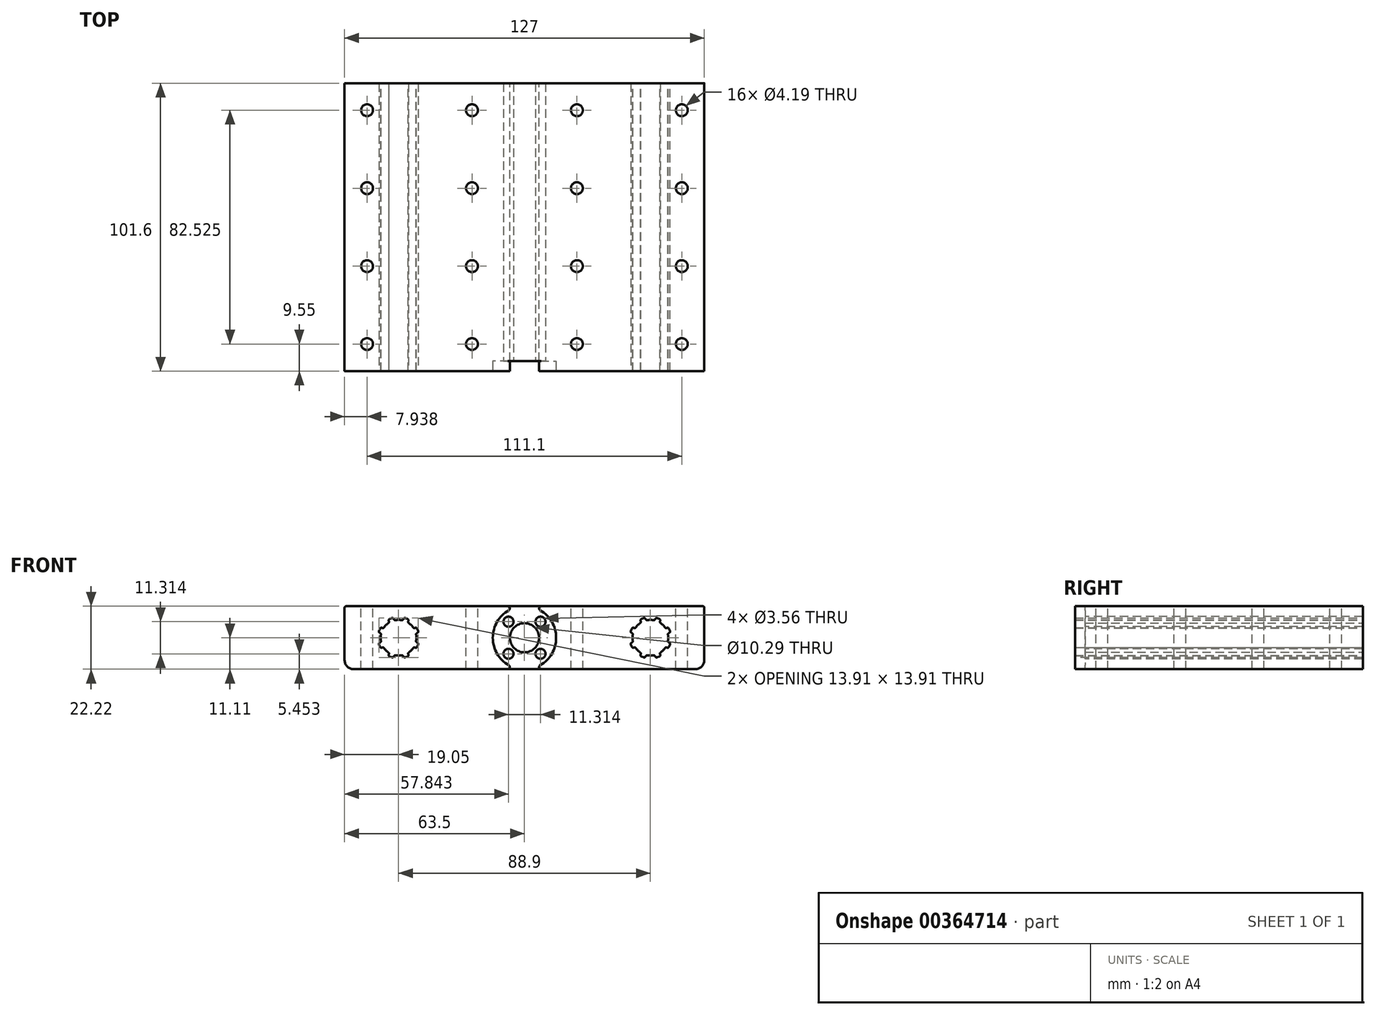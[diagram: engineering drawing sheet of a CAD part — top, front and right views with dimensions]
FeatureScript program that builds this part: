
annotation { "Feature Type Name" : "Feature", "Feature Type Description" : "" }
export const myFeature = defineFeature(function(context is Context, id is Id, definition is map)
    precondition{}
    {
        {
            var Q0;
            Q0=qCreatedBy(makeId("Front.planeOp"),FACE);
            var sketch = newSketch(context, id + "F0", { "sketchPlane" : qUnion([Q0])});
            skCircle(sketch, "E0", {"center": v(0, 0) * mm, "radius": 5.14 * mm});
            skCircle(sketch, "E1", {"center": v(44.45, 0) * mm, "radius": 6.3 * mm});
            skCircle(sketch, "E2", {"center": v(-44.45, 0) * mm, "radius": 6.3 * mm});
            skLineSegment(sketch, "E3", {"start": v(-44.45, 0) * mm, "end": v(0, 0) * mm, "construction": true});
            skLineSegment(sketch, "E4", {"start": v(44.45, 0) * mm, "end": v(0, 0) * mm, "construction": true});
            skLineSegment(sketch, "E5.bottom", {"start": v(-63.5, 11.11) * mm, "end": v(63.5, 11.11) * mm});
            skLineSegment(sketch, "E5.top", {"start": v(-63.5, -11.11) * mm, "end": v(63.5, -11.11) * mm});
            skLineSegment(sketch, "E5.left", {"start": v(-63.5, 11.11) * mm, "end": v(-63.5, -11.11) * mm});
            skLineSegment(sketch, "E5.right", {"start": v(63.5, 11.11) * mm, "end": v(63.5, -11.11) * mm});
            skSolve(sketch);
        }
        {
            var Q0;
            Q0 = qSketchRegion(id + "F0", true);
            extrude(context, id + "F1", {"entities" : qUnion([Q0]), "depth" : 101.6 * mm});
        }
        {
            var Q0;
            Q0=makeQuery(id+"F1.opExtrude","SWEPT_EDGE",EDGE,{"disambiguationData":[OSD([sQuery(id+"F0.wireOp",EDGE,"E5.top"),sQuery(id+"F0.wireOp",EDGE,"E5.left")])]});
            var Q1;
            Q1=makeQuery(id+"F1.opExtrude","SWEPT_EDGE",EDGE,{"disambiguationData":[OSD([sQuery(id+"F0.wireOp",EDGE,"E5.top"),sQuery(id+"F0.wireOp",EDGE,"E5.right")])]});
            fillet(context, id + "F2", {"entities" : qUnion([Q0, Q1]), "radius" : 3.17 * mm, "tangentPropagation" : true, "allowEdgeOverflow" : false});
        }
        {
            var Q0;
            Q0=makeQuery(id+"F1.opExtrude","CAP_FACE",FACE,{"disambiguationData":[OSD([sQuery(id+"F0.wireOp",EDGE,"E0"),sQuery(id+"F0.wireOp",EDGE,"E1"),sQuery(id+"F0.wireOp",EDGE,"E2"),sQuery(id+"F0.wireOp",EDGE,"E5.bottom"),sQuery(id+"F0.wireOp",EDGE,"E5.top"),sQuery(id+"F0.wireOp",EDGE,"E5.left"),sQuery(id+"F0.wireOp",EDGE,"E5.right")])],"isStart":false});
            var sketch = newSketch(context, id + "F3", { "sketchPlane" : qUnion([Q0])});
            skCircle(sketch, "E6", {"center": v(0, 0) * mm, "radius": 8 * mm, "construction": true});
            skCircle(sketch, "E7", {"center": v(-5.66, 5.66) * mm, "radius": 1.78 * mm});
            skCircle(sketch, "E8", {"center": v(5.66, 5.66) * mm, "radius": 1.78 * mm});
            skCircle(sketch, "E9", {"center": v(5.66, -5.66) * mm, "radius": 1.78 * mm});
            skCircle(sketch, "E10", {"center": v(-5.66, -5.66) * mm, "radius": 1.78 * mm});
            skLineSegment(sketch, "E11", {"start": v(-5.66, -5.66) * mm, "end": v(-5.66, 5.66) * mm, "construction": true});
            skLineSegment(sketch, "E12", {"start": v(5.66, 5.66) * mm, "end": v(-5.66, 5.66) * mm, "construction": true});
            skSolve(sketch);
        }
        {
            var Q0;
            Q0 = qSketchRegion(id + "F3", true);
            extrude(context, id + "F4", {"entities" : qUnion([Q0]), "operationType" : NewBodyOperationType.REMOVE, "endBound" : BoundingType.THROUGH_ALL, "oppositeDirection" : true, "depth" : 25.4 * mm});
        }
        {
            var Q0;
            Q0=makeQuery(id+"F1.opExtrude","SWEPT_FACE",FACE,{"disambiguationData":[OSD([sQuery(id+"F0.wireOp",EDGE,"E5.bottom")])]});
            var sketch = newSketch(context, id + "F5", { "sketchPlane" : qUnion([Q0])});
            skCircle(sketch, "E13", {"center": v(-55.56, -9.52) * mm, "radius": 2.1 * mm});
            skCircle(sketch, "E14.0.1.0", {"center": v(-55.56, -37.03) * mm, "radius": 2.1 * mm});
            skCircle(sketch, "E14.0.2.0", {"center": v(-55.56, -64.54) * mm, "radius": 2.1 * mm});
            skCircle(sketch, "E14.0.3.0", {"center": v(-55.56, -92.05) * mm, "radius": 2.1 * mm});
            skCircle(sketch, "E14.1.0.0", {"center": v(-18.53, -9.52) * mm, "radius": 2.1 * mm});
            skCircle(sketch, "E14.1.1.0", {"center": v(-18.53, -37.03) * mm, "radius": 2.1 * mm});
            skCircle(sketch, "E14.1.2.0", {"center": v(-18.53, -64.54) * mm, "radius": 2.1 * mm});
            skCircle(sketch, "E14.1.3.0", {"center": v(-18.53, -92.05) * mm, "radius": 2.1 * mm});
            skCircle(sketch, "E14.2.0.0", {"center": v(18.5, -9.52) * mm, "radius": 2.1 * mm});
            skCircle(sketch, "E14.2.1.0", {"center": v(18.5, -37.03) * mm, "radius": 2.1 * mm});
            skCircle(sketch, "E14.2.2.0", {"center": v(18.5, -64.54) * mm, "radius": 2.1 * mm});
            skCircle(sketch, "E14.2.3.0", {"center": v(18.5, -92.05) * mm, "radius": 2.1 * mm});
            skCircle(sketch, "E14.3.0.0", {"center": v(55.54, -9.52) * mm, "radius": 2.1 * mm});
            skCircle(sketch, "E14.3.1.0", {"center": v(55.54, -37.03) * mm, "radius": 2.1 * mm});
            skCircle(sketch, "E14.3.2.0", {"center": v(55.54, -64.54) * mm, "radius": 2.1 * mm});
            skCircle(sketch, "E14.3.3.0", {"center": v(55.54, -92.05) * mm, "radius": 2.1 * mm});
            skLineSegment(sketch, "E14.direction1", {"start": v(-55.56, -9.53) * mm, "end": v(-18.53, -9.53) * mm, "construction": true});
            skLineSegment(sketch, "E14.direction2", {"start": v(-55.56, -9.52) * mm, "end": v(-55.56, -37.03) * mm, "construction": true});
            skSolve(sketch);
        }
        {
            var Q0;
            Q0 = qSketchRegion(id + "F5", true);
            extrude(context, id + "F6", {"entities" : qUnion([Q0]), "operationType" : NewBodyOperationType.REMOVE, "oppositeDirection" : true, "depth" : 25.4 * mm, "offsetDistance" : 25.4 * mm});
        }
        {
            var Q0;
            Q0=makeQuery(id+"F1.opExtrude","CAP_FACE",FACE,{"disambiguationData":[OSD([sQuery(id+"F0.wireOp",EDGE,"E0"),sQuery(id+"F0.wireOp",EDGE,"E1"),sQuery(id+"F0.wireOp",EDGE,"E2"),sQuery(id+"F0.wireOp",EDGE,"E5.bottom"),sQuery(id+"F0.wireOp",EDGE,"E5.top"),sQuery(id+"F0.wireOp",EDGE,"E5.left"),sQuery(id+"F0.wireOp",EDGE,"E5.right")])],"isStart":false});
            var sketch = newSketch(context, id + "F7", { "sketchPlane" : qUnion([Q0])});
            skLineSegment(sketch, "E15.bottom", {"start": v(-50.83, 3.67) * mm, "end": v(-37.34, -1.91) * mm});
            skLineSegment(sketch, "E15.top", {"start": v(-51.56, 1.91) * mm, "end": v(-38.07, -3.67) * mm});
            skLineSegment(sketch, "E15.left", {"start": v(-50.83, 3.67) * mm, "end": v(-51.56, 1.91) * mm});
            skLineSegment(sketch, "E15.right", {"start": v(-37.34, -1.91) * mm, "end": v(-38.07, -3.67) * mm});
            skPoint(sketch, "E15.middle", {"position": v(-44.45, 0) * mm});
            skLineSegment(sketch, "E16", {"start": v(-44.45, 0) * mm, "end": v(-54.68, 0) * mm, "construction": true});
            skLineSegment(sketch, "E17.1.0", {"start": v(-46.36, 7.11) * mm, "end": v(-40.78, -6.38) * mm});
            skLineSegment(sketch, "E17.1.1", {"start": v(-40.78, -6.38) * mm, "end": v(-42.54, -7.11) * mm});
            skLineSegment(sketch, "E17.1.2", {"start": v(-48.12, 6.38) * mm, "end": v(-42.54, -7.11) * mm});
            skLineSegment(sketch, "E17.1.3", {"start": v(-46.36, 7.11) * mm, "end": v(-48.12, 6.38) * mm});
            skLineSegment(sketch, "E17.2.0", {"start": v(-40.78, 6.38) * mm, "end": v(-46.36, -7.11) * mm});
            skLineSegment(sketch, "E17.2.1", {"start": v(-46.36, -7.11) * mm, "end": v(-48.12, -6.38) * mm});
            skLineSegment(sketch, "E17.2.2", {"start": v(-42.54, 7.11) * mm, "end": v(-48.12, -6.38) * mm});
            skLineSegment(sketch, "E17.2.3", {"start": v(-40.78, 6.38) * mm, "end": v(-42.54, 7.11) * mm});
            skLineSegment(sketch, "E17.3.0", {"start": v(-37.34, 1.91) * mm, "end": v(-50.83, -3.67) * mm});
            skLineSegment(sketch, "E17.3.1", {"start": v(-50.83, -3.67) * mm, "end": v(-51.56, -1.91) * mm});
            skLineSegment(sketch, "E17.3.2", {"start": v(-38.07, 3.67) * mm, "end": v(-51.56, -1.91) * mm});
            skLineSegment(sketch, "E17.3.3", {"start": v(-37.34, 1.91) * mm, "end": v(-38.07, 3.67) * mm});
            skLineSegment(sketch, "E17.anchor1", {"start": v(-44.45, 0) * mm, "end": v(-50.83, 3.67) * mm, "construction": true});
            skLineSegment(sketch, "E17.anchor2", {"start": v(-44.45, 0) * mm, "end": v(-37.34, 1.91) * mm, "construction": true});
            skLineSegment(sketch, "E18.1.0.0", {"start": v(37.34, 1.91) * mm, "end": v(50.83, -3.67) * mm});
            skLineSegment(sketch, "E18.1.0.1", {"start": v(50.83, 3.67) * mm, "end": v(37.34, -1.91) * mm});
            skPoint(sketch, "E18.1.0.2", {"position": v(44.45, 0) * mm});
            skLineSegment(sketch, "E18.1.0.3", {"start": v(51.56, 1.91) * mm, "end": v(38.07, -3.67) * mm});
            skLineSegment(sketch, "E18.1.0.4", {"start": v(38.07, 3.67) * mm, "end": v(51.56, -1.91) * mm});
            skLineSegment(sketch, "E18.1.0.5", {"start": v(44.45, 0) * mm, "end": v(34.22, 0) * mm, "construction": true});
            skLineSegment(sketch, "E18.1.0.6", {"start": v(42.54, 7.11) * mm, "end": v(48.12, -6.38) * mm});
            skLineSegment(sketch, "E18.1.0.7", {"start": v(40.78, 6.38) * mm, "end": v(46.36, -7.11) * mm});
            skLineSegment(sketch, "E18.1.0.8", {"start": v(44.45, 0) * mm, "end": v(51.56, 1.91) * mm, "construction": true});
            skLineSegment(sketch, "E18.1.0.9", {"start": v(48.12, 6.38) * mm, "end": v(42.54, -7.11) * mm});
            skLineSegment(sketch, "E18.1.0.10", {"start": v(46.36, 7.11) * mm, "end": v(40.78, -6.38) * mm});
            skLineSegment(sketch, "E18.1.0.11", {"start": v(44.45, 0) * mm, "end": v(38.07, 3.67) * mm, "construction": true});
            skPoint(sketch, "E18.1.0.12", {"position": v(44.45, 0) * mm});
            skLineSegment(sketch, "E18.1.0.13", {"start": v(38.07, -3.67) * mm, "end": v(37.34, -1.91) * mm});
            skLineSegment(sketch, "E18.1.0.14", {"start": v(51.56, 1.91) * mm, "end": v(50.83, 3.67) * mm});
            skLineSegment(sketch, "E18.1.0.15", {"start": v(38.07, 3.67) * mm, "end": v(37.34, 1.91) * mm});
            skLineSegment(sketch, "E18.1.0.16", {"start": v(51.56, -1.91) * mm, "end": v(50.83, -3.67) * mm});
            skLineSegment(sketch, "E18.1.0.17", {"start": v(48.12, -6.38) * mm, "end": v(46.36, -7.11) * mm});
            skLineSegment(sketch, "E18.1.0.18", {"start": v(42.54, 7.11) * mm, "end": v(40.78, 6.38) * mm});
            skLineSegment(sketch, "E18.1.0.19", {"start": v(42.54, -7.11) * mm, "end": v(40.78, -6.38) * mm});
            skLineSegment(sketch, "E18.1.0.20", {"start": v(48.12, 6.38) * mm, "end": v(46.36, 7.11) * mm});
            skLineSegment(sketch, "E18.direction1", {"start": v(-54.68, 0) * mm, "end": v(34.22, 0) * mm, "construction": true});
            skSolve(sketch);
        }
        {
            var Q0;
            Q0 = qSketchRegion(id + "F7", true);
            extrude(context, id + "F8", {"entities" : qUnion([Q0]), "operationType" : NewBodyOperationType.REMOVE, "endBound" : BoundingType.THROUGH_ALL, "oppositeDirection" : true, "depth" : 25.4 * mm, "offsetDistance" : 25.4 * mm});
        }
        {
            var Q0;
            {var subQ0=sQuery(id+"F7.wireOp",EDGE,"E17.2.2");var subQ1=sQuery(id+"F0.wireOp",EDGE,"E2");Q0=makeQuery(id+"F8.boolean.opBoolean","INTERSECT",EDGE,{"derivedFrom":[makeQuery(id+"F1.opExtrude","SWEPT_FACE",FACE,{"disambiguationData":[OSD([subQ1])]}),makeQuery(id+"F8.opExtrude","SWEPT_FACE",FACE,{"disambiguationData":[OSD([subQ0]),TDD([makeQuery(id+"F7.imprint","IMPRINT",EDGE,{"disambiguationData":[TD([[makeQuery(id+"F7.imprint","INTERSECT",VERTEX,{"derivedFrom":[subQ0,sQuery(id+"F7.wireOp",EDGE,"E17.2.3")]}),-1.0]])],"derivedFrom":subQ0}),makeQuery(id+"F7.imprint","IMPRINT",EDGE,{"disambiguationData":[TD([[makeQuery(id+"F7.imprint","INTERSECT",VERTEX,{"derivedFrom":[sQuery(id+"F7.wireOp",EDGE,"E17.1.0"),subQ0]}),1.0]])],"derivedFrom":subQ0})])]})]});}
            var Q1;
            {var subQ0=sQuery(id+"F7.wireOp",EDGE,"E17.1.0");var subQ1=sQuery(id+"F0.wireOp",EDGE,"E2");Q1=makeQuery(id+"F8.boolean.opBoolean","INTERSECT",EDGE,{"derivedFrom":[makeQuery(id+"F1.opExtrude","SWEPT_FACE",FACE,{"disambiguationData":[OSD([subQ1])]}),makeQuery(id+"F8.opExtrude","SWEPT_FACE",FACE,{"disambiguationData":[OSD([subQ0]),TDD([makeQuery(id+"F7.imprint","IMPRINT",EDGE,{"disambiguationData":[TD([[makeQuery(id+"F7.imprint","INTERSECT",VERTEX,{"derivedFrom":[subQ0,sQuery(id+"F7.wireOp",EDGE,"E17.1.3")]}),-1.0]])],"derivedFrom":subQ0}),makeQuery(id+"F7.imprint","IMPRINT",EDGE,{"disambiguationData":[TD([[makeQuery(id+"F7.imprint","INTERSECT",VERTEX,{"derivedFrom":[subQ0,sQuery(id+"F7.wireOp",EDGE,"E17.2.2")]}),1.0]])],"derivedFrom":subQ0})])]})]});}
            var Q2;
            Q2=makeQuery(id+"F8.boolean.opBoolean","COPY",EDGE,{"derivedFrom":makeQuery(id+"F8.opExtrude","SWEPT_EDGE",EDGE,{"disambiguationData":[OSD([sQuery(id+"F7.wireOp",EDGE,"E17.1.0"),sQuery(id+"F7.wireOp",EDGE,"E17.1.3")])]})});
            var Q3;
            Q3=makeQuery(id+"F8.boolean.opBoolean","COPY",EDGE,{"derivedFrom":makeQuery(id+"F8.opExtrude","SWEPT_EDGE",EDGE,{"disambiguationData":[OSD([sQuery(id+"F7.wireOp",EDGE,"E17.1.2"),sQuery(id+"F7.wireOp",EDGE,"E17.1.3")])]})});
            var Q4;
            {var subQ0=sQuery(id+"F7.wireOp",EDGE,"E17.1.2");var subQ1=sQuery(id+"F0.wireOp",EDGE,"E2");Q4=makeQuery(id+"F8.boolean.opBoolean","INTERSECT",EDGE,{"derivedFrom":[makeQuery(id+"F1.opExtrude","SWEPT_FACE",FACE,{"disambiguationData":[OSD([subQ1])]}),makeQuery(id+"F8.opExtrude","SWEPT_FACE",FACE,{"disambiguationData":[OSD([subQ0]),TDD([makeQuery(id+"F7.imprint","IMPRINT",EDGE,{"disambiguationData":[TD([[makeQuery(id+"F7.imprint","INTERSECT",VERTEX,{"derivedFrom":[subQ0,sQuery(id+"F7.wireOp",EDGE,"E17.1.3")]}),-1.0]])],"derivedFrom":subQ0}),makeQuery(id+"F7.imprint","IMPRINT",EDGE,{"disambiguationData":[TD([[makeQuery(id+"F7.imprint","INTERSECT",VERTEX,{"derivedFrom":[sQuery(id+"F7.wireOp",EDGE,"E15.bottom"),subQ0]}),1.0]])],"derivedFrom":subQ0})])]})]});}
            var Q5;
            {var subQ0=sQuery(id+"F7.wireOp",EDGE,"E15.bottom");var subQ1=sQuery(id+"F0.wireOp",EDGE,"E2");Q5=makeQuery(id+"F8.boolean.opBoolean","INTERSECT",EDGE,{"derivedFrom":[makeQuery(id+"F1.opExtrude","SWEPT_FACE",FACE,{"disambiguationData":[OSD([subQ1])]}),makeQuery(id+"F8.opExtrude","SWEPT_FACE",FACE,{"disambiguationData":[OSD([subQ0]),TDD([makeQuery(id+"F7.imprint","IMPRINT",EDGE,{"disambiguationData":[TD([[makeQuery(id+"F7.imprint","INTERSECT",VERTEX,{"derivedFrom":[subQ0,sQuery(id+"F7.wireOp",EDGE,"E15.left")]}),-1.0]])],"derivedFrom":subQ0}),makeQuery(id+"F7.imprint","IMPRINT",EDGE,{"disambiguationData":[TD([[makeQuery(id+"F7.imprint","INTERSECT",VERTEX,{"derivedFrom":[subQ0,sQuery(id+"F7.wireOp",EDGE,"E17.1.2")]}),1.0]])],"derivedFrom":subQ0})])]})]});}
            var Q6;
            Q6=makeQuery(id+"F8.boolean.opBoolean","COPY",EDGE,{"derivedFrom":makeQuery(id+"F8.opExtrude","SWEPT_EDGE",EDGE,{"disambiguationData":[OSD([sQuery(id+"F7.wireOp",EDGE,"E15.bottom"),sQuery(id+"F7.wireOp",EDGE,"E15.left")])]})});
            var Q7;
            Q7=makeQuery(id+"F8.boolean.opBoolean","COPY",EDGE,{"derivedFrom":makeQuery(id+"F8.opExtrude","SWEPT_EDGE",EDGE,{"disambiguationData":[OSD([sQuery(id+"F7.wireOp",EDGE,"E15.top"),sQuery(id+"F7.wireOp",EDGE,"E15.left")])]})});
            var Q8;
            {var subQ0=sQuery(id+"F7.wireOp",EDGE,"E15.top");var subQ1=sQuery(id+"F0.wireOp",EDGE,"E2");Q8=makeQuery(id+"F8.boolean.opBoolean","INTERSECT",EDGE,{"derivedFrom":[makeQuery(id+"F1.opExtrude","SWEPT_FACE",FACE,{"disambiguationData":[OSD([subQ1])]}),makeQuery(id+"F8.opExtrude","SWEPT_FACE",FACE,{"disambiguationData":[OSD([subQ0]),TDD([makeQuery(id+"F7.imprint","IMPRINT",EDGE,{"disambiguationData":[TD([[makeQuery(id+"F7.imprint","INTERSECT",VERTEX,{"derivedFrom":[subQ0,sQuery(id+"F7.wireOp",EDGE,"E15.left")]}),-1.0]])],"derivedFrom":subQ0}),makeQuery(id+"F7.imprint","IMPRINT",EDGE,{"disambiguationData":[TD([[makeQuery(id+"F7.imprint","INTERSECT",VERTEX,{"derivedFrom":[subQ0,sQuery(id+"F7.wireOp",EDGE,"E17.3.2")]}),1.0]])],"derivedFrom":subQ0})])]})]});}
            var Q9;
            {var subQ0=sQuery(id+"F7.wireOp",EDGE,"E17.3.2");var subQ1=sQuery(id+"F0.wireOp",EDGE,"E2");Q9=makeQuery(id+"F8.boolean.opBoolean","INTERSECT",EDGE,{"derivedFrom":[makeQuery(id+"F1.opExtrude","SWEPT_FACE",FACE,{"disambiguationData":[OSD([subQ1])]}),makeQuery(id+"F8.opExtrude","SWEPT_FACE",FACE,{"disambiguationData":[OSD([subQ0]),TDD([makeQuery(id+"F7.imprint","IMPRINT",EDGE,{"disambiguationData":[TD([[makeQuery(id+"F7.imprint","INTERSECT",VERTEX,{"derivedFrom":[sQuery(id+"F7.wireOp",EDGE,"E15.top"),subQ0]}),-1.0]])],"derivedFrom":subQ0}),makeQuery(id+"F7.imprint","IMPRINT",EDGE,{"disambiguationData":[TD([[makeQuery(id+"F7.imprint","INTERSECT",VERTEX,{"derivedFrom":[sQuery(id+"F7.wireOp",EDGE,"E17.3.1"),subQ0]}),1.0]])],"derivedFrom":subQ0})])]})]});}
            var Q10;
            Q10=makeQuery(id+"F8.boolean.opBoolean","COPY",EDGE,{"derivedFrom":makeQuery(id+"F8.opExtrude","SWEPT_EDGE",EDGE,{"disambiguationData":[OSD([sQuery(id+"F7.wireOp",EDGE,"E17.3.1"),sQuery(id+"F7.wireOp",EDGE,"E17.3.2")])]})});
            var Q11;
            Q11=makeQuery(id+"F8.boolean.opBoolean","COPY",EDGE,{"derivedFrom":makeQuery(id+"F8.opExtrude","SWEPT_EDGE",EDGE,{"disambiguationData":[OSD([sQuery(id+"F7.wireOp",EDGE,"E17.3.0"),sQuery(id+"F7.wireOp",EDGE,"E17.3.1")])]})});
            var Q12;
            {var subQ0=sQuery(id+"F7.wireOp",EDGE,"E17.3.0");var subQ1=sQuery(id+"F0.wireOp",EDGE,"E2");Q12=makeQuery(id+"F8.boolean.opBoolean","INTERSECT",EDGE,{"derivedFrom":[makeQuery(id+"F1.opExtrude","SWEPT_FACE",FACE,{"disambiguationData":[OSD([subQ1])]}),makeQuery(id+"F8.opExtrude","SWEPT_FACE",FACE,{"disambiguationData":[OSD([subQ0]),TDD([makeQuery(id+"F7.imprint","IMPRINT",EDGE,{"disambiguationData":[TD([[makeQuery(id+"F7.imprint","INTERSECT",VERTEX,{"derivedFrom":[sQuery(id+"F7.wireOp",EDGE,"E17.2.2"),subQ0]}),-1.0]])],"derivedFrom":subQ0}),makeQuery(id+"F7.imprint","IMPRINT",EDGE,{"disambiguationData":[TD([[makeQuery(id+"F7.imprint","INTERSECT",VERTEX,{"derivedFrom":[subQ0,sQuery(id+"F7.wireOp",EDGE,"E17.3.1")]}),1.0]])],"derivedFrom":subQ0})])]})]});}
            var Q13;
            Q13=makeQuery(id+"F8.boolean.opBoolean","COPY",EDGE,{"derivedFrom":makeQuery(id+"F8.opExtrude","SWEPT_EDGE",EDGE,{"disambiguationData":[OSD([sQuery(id+"F7.wireOp",EDGE,"E17.2.1"),sQuery(id+"F7.wireOp",EDGE,"E17.2.2")])]})});
            var Q14;
            {var subQ0=sQuery(id+"F7.wireOp",EDGE,"E17.2.2");var subQ1=sQuery(id+"F0.wireOp",EDGE,"E2");Q14=makeQuery(id+"F8.boolean.opBoolean","INTERSECT",EDGE,{"derivedFrom":[makeQuery(id+"F1.opExtrude","SWEPT_FACE",FACE,{"disambiguationData":[OSD([subQ1])]}),makeQuery(id+"F8.opExtrude","SWEPT_FACE",FACE,{"disambiguationData":[OSD([subQ0]),TDD([makeQuery(id+"F7.imprint","IMPRINT",EDGE,{"disambiguationData":[TD([[makeQuery(id+"F7.imprint","INTERSECT",VERTEX,{"derivedFrom":[subQ0,sQuery(id+"F7.wireOp",EDGE,"E17.3.0")]}),-1.0]])],"derivedFrom":subQ0}),makeQuery(id+"F7.imprint","IMPRINT",EDGE,{"disambiguationData":[TD([[makeQuery(id+"F7.imprint","INTERSECT",VERTEX,{"derivedFrom":[sQuery(id+"F7.wireOp",EDGE,"E17.2.1"),subQ0]}),1.0]])],"derivedFrom":subQ0})])]})]});}
            var Q15;
            Q15=makeQuery(id+"F8.boolean.opBoolean","COPY",EDGE,{"derivedFrom":makeQuery(id+"F8.opExtrude","SWEPT_EDGE",EDGE,{"disambiguationData":[OSD([sQuery(id+"F7.wireOp",EDGE,"E17.2.0"),sQuery(id+"F7.wireOp",EDGE,"E17.2.1")])]})});
            var Q16;
            {var subQ0=sQuery(id+"F7.wireOp",EDGE,"E17.2.0");var subQ1=sQuery(id+"F0.wireOp",EDGE,"E2");Q16=makeQuery(id+"F8.boolean.opBoolean","INTERSECT",EDGE,{"derivedFrom":[makeQuery(id+"F1.opExtrude","SWEPT_FACE",FACE,{"disambiguationData":[OSD([subQ1])]}),makeQuery(id+"F8.opExtrude","SWEPT_FACE",FACE,{"disambiguationData":[OSD([subQ0]),TDD([makeQuery(id+"F7.imprint","IMPRINT",EDGE,{"disambiguationData":[TD([[makeQuery(id+"F7.imprint","INTERSECT",VERTEX,{"derivedFrom":[sQuery(id+"F7.wireOp",EDGE,"E17.1.2"),subQ0]}),-1.0]])],"derivedFrom":subQ0}),makeQuery(id+"F7.imprint","IMPRINT",EDGE,{"disambiguationData":[TD([[makeQuery(id+"F7.imprint","INTERSECT",VERTEX,{"derivedFrom":[subQ0,sQuery(id+"F7.wireOp",EDGE,"E17.2.1")]}),1.0]])],"derivedFrom":subQ0})])]})]});}
            var Q17;
            Q17=makeQuery(id+"F8.boolean.opBoolean","COPY",EDGE,{"derivedFrom":makeQuery(id+"F8.opExtrude","SWEPT_EDGE",EDGE,{"disambiguationData":[OSD([sQuery(id+"F7.wireOp",EDGE,"E17.1.1"),sQuery(id+"F7.wireOp",EDGE,"E17.1.2")])]})});
            var Q18;
            {var subQ0=sQuery(id+"F7.wireOp",EDGE,"E17.1.2");var subQ1=sQuery(id+"F0.wireOp",EDGE,"E2");Q18=makeQuery(id+"F8.boolean.opBoolean","INTERSECT",EDGE,{"derivedFrom":[makeQuery(id+"F1.opExtrude","SWEPT_FACE",FACE,{"disambiguationData":[OSD([subQ1])]}),makeQuery(id+"F8.opExtrude","SWEPT_FACE",FACE,{"disambiguationData":[OSD([subQ0]),TDD([makeQuery(id+"F7.imprint","IMPRINT",EDGE,{"disambiguationData":[TD([[makeQuery(id+"F7.imprint","INTERSECT",VERTEX,{"derivedFrom":[subQ0,sQuery(id+"F7.wireOp",EDGE,"E17.2.0")]}),-1.0]])],"derivedFrom":subQ0}),makeQuery(id+"F7.imprint","IMPRINT",EDGE,{"disambiguationData":[TD([[makeQuery(id+"F7.imprint","INTERSECT",VERTEX,{"derivedFrom":[sQuery(id+"F7.wireOp",EDGE,"E17.1.1"),subQ0]}),1.0]])],"derivedFrom":subQ0})])]})]});}
            var Q19;
            Q19=makeQuery(id+"F8.boolean.opBoolean","COPY",EDGE,{"derivedFrom":makeQuery(id+"F8.opExtrude","SWEPT_EDGE",EDGE,{"disambiguationData":[OSD([sQuery(id+"F7.wireOp",EDGE,"E17.1.0"),sQuery(id+"F7.wireOp",EDGE,"E17.1.1")])]})});
            var Q20;
            {var subQ0=sQuery(id+"F7.wireOp",EDGE,"E17.1.0");var subQ1=sQuery(id+"F0.wireOp",EDGE,"E2");Q20=makeQuery(id+"F8.boolean.opBoolean","INTERSECT",EDGE,{"derivedFrom":[makeQuery(id+"F1.opExtrude","SWEPT_FACE",FACE,{"disambiguationData":[OSD([subQ1])]}),makeQuery(id+"F8.opExtrude","SWEPT_FACE",FACE,{"disambiguationData":[OSD([subQ0]),TDD([makeQuery(id+"F7.imprint","IMPRINT",EDGE,{"disambiguationData":[TD([[makeQuery(id+"F7.imprint","INTERSECT",VERTEX,{"derivedFrom":[sQuery(id+"F7.wireOp",EDGE,"E15.top"),subQ0]}),-1.0]])],"derivedFrom":subQ0}),makeQuery(id+"F7.imprint","IMPRINT",EDGE,{"disambiguationData":[TD([[makeQuery(id+"F7.imprint","INTERSECT",VERTEX,{"derivedFrom":[subQ0,sQuery(id+"F7.wireOp",EDGE,"E17.1.1")]}),1.0]])],"derivedFrom":subQ0})])]})]});}
            var Q21;
            Q21=makeQuery(id+"F8.boolean.opBoolean","COPY",EDGE,{"derivedFrom":makeQuery(id+"F8.opExtrude","SWEPT_EDGE",EDGE,{"disambiguationData":[OSD([sQuery(id+"F7.wireOp",EDGE,"E15.top"),sQuery(id+"F7.wireOp",EDGE,"E15.right")])]})});
            var Q22;
            {var subQ0=sQuery(id+"F7.wireOp",EDGE,"E15.top");var subQ1=sQuery(id+"F0.wireOp",EDGE,"E2");Q22=makeQuery(id+"F8.boolean.opBoolean","INTERSECT",EDGE,{"derivedFrom":[makeQuery(id+"F1.opExtrude","SWEPT_FACE",FACE,{"disambiguationData":[OSD([subQ1])]}),makeQuery(id+"F8.opExtrude","SWEPT_FACE",FACE,{"disambiguationData":[OSD([subQ0]),TDD([makeQuery(id+"F7.imprint","IMPRINT",EDGE,{"disambiguationData":[TD([[makeQuery(id+"F7.imprint","INTERSECT",VERTEX,{"derivedFrom":[subQ0,sQuery(id+"F7.wireOp",EDGE,"E17.1.0")]}),-1.0]])],"derivedFrom":subQ0}),makeQuery(id+"F7.imprint","IMPRINT",EDGE,{"disambiguationData":[TD([[makeQuery(id+"F7.imprint","INTERSECT",VERTEX,{"derivedFrom":[subQ0,sQuery(id+"F7.wireOp",EDGE,"E15.right")]}),1.0]])],"derivedFrom":subQ0})])]})]});}
            var Q23;
            Q23=makeQuery(id+"F8.boolean.opBoolean","COPY",EDGE,{"derivedFrom":makeQuery(id+"F8.opExtrude","SWEPT_EDGE",EDGE,{"disambiguationData":[OSD([sQuery(id+"F7.wireOp",EDGE,"E15.bottom"),sQuery(id+"F7.wireOp",EDGE,"E15.right")])]})});
            var Q24;
            {var subQ0=sQuery(id+"F7.wireOp",EDGE,"E15.bottom");var subQ1=sQuery(id+"F0.wireOp",EDGE,"E2");Q24=makeQuery(id+"F8.boolean.opBoolean","INTERSECT",EDGE,{"derivedFrom":[makeQuery(id+"F1.opExtrude","SWEPT_FACE",FACE,{"disambiguationData":[OSD([subQ1])]}),makeQuery(id+"F8.opExtrude","SWEPT_FACE",FACE,{"disambiguationData":[OSD([subQ0]),TDD([makeQuery(id+"F7.imprint","IMPRINT",EDGE,{"disambiguationData":[TD([[makeQuery(id+"F7.imprint","INTERSECT",VERTEX,{"derivedFrom":[subQ0,sQuery(id+"F7.wireOp",EDGE,"E17.3.0")]}),-1.0]])],"derivedFrom":subQ0}),makeQuery(id+"F7.imprint","IMPRINT",EDGE,{"disambiguationData":[TD([[makeQuery(id+"F7.imprint","INTERSECT",VERTEX,{"derivedFrom":[subQ0,sQuery(id+"F7.wireOp",EDGE,"E15.right")]}),1.0]])],"derivedFrom":subQ0})])]})]});}
            var Q25;
            {var subQ0=sQuery(id+"F7.wireOp",EDGE,"E17.3.0");var subQ1=sQuery(id+"F0.wireOp",EDGE,"E2");Q25=makeQuery(id+"F8.boolean.opBoolean","INTERSECT",EDGE,{"derivedFrom":[makeQuery(id+"F1.opExtrude","SWEPT_FACE",FACE,{"disambiguationData":[OSD([subQ1])]}),makeQuery(id+"F8.opExtrude","SWEPT_FACE",FACE,{"disambiguationData":[OSD([subQ0]),TDD([makeQuery(id+"F7.imprint","IMPRINT",EDGE,{"disambiguationData":[TD([[makeQuery(id+"F7.imprint","INTERSECT",VERTEX,{"derivedFrom":[subQ0,sQuery(id+"F7.wireOp",EDGE,"E17.3.3")]}),-1.0]])],"derivedFrom":subQ0}),makeQuery(id+"F7.imprint","IMPRINT",EDGE,{"disambiguationData":[TD([[makeQuery(id+"F7.imprint","INTERSECT",VERTEX,{"derivedFrom":[sQuery(id+"F7.wireOp",EDGE,"E15.bottom"),subQ0]}),1.0]])],"derivedFrom":subQ0})])]})]});}
            var Q26;
            Q26=makeQuery(id+"F8.boolean.opBoolean","COPY",EDGE,{"derivedFrom":makeQuery(id+"F8.opExtrude","SWEPT_EDGE",EDGE,{"disambiguationData":[OSD([sQuery(id+"F7.wireOp",EDGE,"E17.3.0"),sQuery(id+"F7.wireOp",EDGE,"E17.3.3")])]})});
            var Q27;
            Q27=makeQuery(id+"F8.boolean.opBoolean","COPY",EDGE,{"derivedFrom":makeQuery(id+"F8.opExtrude","SWEPT_EDGE",EDGE,{"disambiguationData":[OSD([sQuery(id+"F7.wireOp",EDGE,"E17.3.2"),sQuery(id+"F7.wireOp",EDGE,"E17.3.3")])]})});
            var Q28;
            {var subQ0=sQuery(id+"F7.wireOp",EDGE,"E17.3.2");var subQ1=sQuery(id+"F0.wireOp",EDGE,"E2");Q28=makeQuery(id+"F8.boolean.opBoolean","INTERSECT",EDGE,{"derivedFrom":[makeQuery(id+"F1.opExtrude","SWEPT_FACE",FACE,{"disambiguationData":[OSD([subQ1])]}),makeQuery(id+"F8.opExtrude","SWEPT_FACE",FACE,{"disambiguationData":[OSD([subQ0]),TDD([makeQuery(id+"F7.imprint","IMPRINT",EDGE,{"disambiguationData":[TD([[makeQuery(id+"F7.imprint","INTERSECT",VERTEX,{"derivedFrom":[subQ0,sQuery(id+"F7.wireOp",EDGE,"E17.3.3")]}),-1.0]])],"derivedFrom":subQ0}),makeQuery(id+"F7.imprint","IMPRINT",EDGE,{"disambiguationData":[TD([[makeQuery(id+"F7.imprint","INTERSECT",VERTEX,{"derivedFrom":[sQuery(id+"F7.wireOp",EDGE,"E17.2.0"),subQ0]}),1.0]])],"derivedFrom":subQ0})])]})]});}
            var Q29;
            Q29=makeQuery(id+"F8.boolean.opBoolean","COPY",EDGE,{"derivedFrom":makeQuery(id+"F8.opExtrude","SWEPT_EDGE",EDGE,{"disambiguationData":[OSD([sQuery(id+"F7.wireOp",EDGE,"E17.2.0"),sQuery(id+"F7.wireOp",EDGE,"E17.2.3")])]})});
            var Q30;
            {var subQ0=sQuery(id+"F7.wireOp",EDGE,"E17.2.0");var subQ1=sQuery(id+"F0.wireOp",EDGE,"E2");Q30=makeQuery(id+"F8.boolean.opBoolean","INTERSECT",EDGE,{"derivedFrom":[makeQuery(id+"F1.opExtrude","SWEPT_FACE",FACE,{"disambiguationData":[OSD([subQ1])]}),makeQuery(id+"F8.opExtrude","SWEPT_FACE",FACE,{"disambiguationData":[OSD([subQ0]),TDD([makeQuery(id+"F7.imprint","IMPRINT",EDGE,{"disambiguationData":[TD([[makeQuery(id+"F7.imprint","INTERSECT",VERTEX,{"derivedFrom":[subQ0,sQuery(id+"F7.wireOp",EDGE,"E17.2.3")]}),-1.0]])],"derivedFrom":subQ0}),makeQuery(id+"F7.imprint","IMPRINT",EDGE,{"disambiguationData":[TD([[makeQuery(id+"F7.imprint","INTERSECT",VERTEX,{"derivedFrom":[subQ0,sQuery(id+"F7.wireOp",EDGE,"E17.3.2")]}),1.0]])],"derivedFrom":subQ0})])]})]});}
            var Q31;
            Q31=makeQuery(id+"F8.boolean.opBoolean","COPY",EDGE,{"derivedFrom":makeQuery(id+"F8.opExtrude","SWEPT_EDGE",EDGE,{"disambiguationData":[OSD([sQuery(id+"F7.wireOp",EDGE,"E17.2.2"),sQuery(id+"F7.wireOp",EDGE,"E17.2.3")])]})});
            fillet(context, id + "F9", {"entities" : qUnion([Q0, Q1, Q2, Q3, Q4, Q5, Q6, Q7, Q8, Q9, Q10, Q11, Q12, Q13, Q14, Q15, Q16, Q17, Q18, Q19, Q20, Q21, Q22, Q23, Q24, Q25, Q26, Q27, Q28, Q29, Q30, Q31]), "radius" : 0.5 * mm, "allowEdgeOverflow" : false});
        }
        {
            var Q0;
            Q0=makeQuery(id+"F8.boolean.opBoolean","COPY",EDGE,{"derivedFrom":makeQuery(id+"F8.opExtrude","SWEPT_EDGE",EDGE,{"disambiguationData":[OSD([sQuery(id+"F7.wireOp",EDGE,"E18.1.0.7"),sQuery(id+"F7.wireOp",EDGE,"E18.1.0.17")])]})});
            var Q1;
            {var subQ0=sQuery(id+"F7.wireOp",EDGE,"E18.1.0.7");var subQ1=sQuery(id+"F0.wireOp",EDGE,"E1");Q1=makeQuery(id+"F8.boolean.opBoolean","INTERSECT",EDGE,{"derivedFrom":[makeQuery(id+"F1.opExtrude","SWEPT_FACE",FACE,{"disambiguationData":[OSD([subQ1])]}),makeQuery(id+"F8.opExtrude","SWEPT_FACE",FACE,{"disambiguationData":[OSD([subQ0]),TDD([makeQuery(id+"F7.imprint","IMPRINT",EDGE,{"disambiguationData":[TD([[makeQuery(id+"F7.imprint","INTERSECT",VERTEX,{"derivedFrom":[subQ0,sQuery(id+"F7.wireOp",EDGE,"E18.1.0.9")]}),-1.0]])],"derivedFrom":subQ0}),makeQuery(id+"F7.imprint","IMPRINT",EDGE,{"disambiguationData":[TD([[makeQuery(id+"F7.imprint","INTERSECT",VERTEX,{"derivedFrom":[subQ0,sQuery(id+"F7.wireOp",EDGE,"E18.1.0.17")]}),1.0]])],"derivedFrom":subQ0})])]})]});}
            var Q2;
            {var subQ0=sQuery(id+"F7.wireOp",EDGE,"E18.1.0.9");var subQ1=sQuery(id+"F0.wireOp",EDGE,"E1");Q2=makeQuery(id+"F8.boolean.opBoolean","INTERSECT",EDGE,{"derivedFrom":[makeQuery(id+"F1.opExtrude","SWEPT_FACE",FACE,{"disambiguationData":[OSD([subQ1])]}),makeQuery(id+"F8.opExtrude","SWEPT_FACE",FACE,{"disambiguationData":[OSD([subQ0]),TDD([makeQuery(id+"F7.imprint","IMPRINT",EDGE,{"disambiguationData":[TD([[makeQuery(id+"F7.imprint","INTERSECT",VERTEX,{"derivedFrom":[sQuery(id+"F7.wireOp",EDGE,"E18.1.0.7"),subQ0]}),-1.0]])],"derivedFrom":subQ0}),makeQuery(id+"F7.imprint","IMPRINT",EDGE,{"disambiguationData":[TD([[makeQuery(id+"F7.imprint","INTERSECT",VERTEX,{"derivedFrom":[subQ0,sQuery(id+"F7.wireOp",EDGE,"E18.1.0.19")]}),1.0]])],"derivedFrom":subQ0})])]})]});}
            var Q3;
            {var subQ0=sQuery(id+"F7.wireOp",EDGE,"E18.1.0.10");var subQ1=sQuery(id+"F0.wireOp",EDGE,"E1");Q3=makeQuery(id+"F8.boolean.opBoolean","INTERSECT",EDGE,{"derivedFrom":[makeQuery(id+"F1.opExtrude","SWEPT_FACE",FACE,{"disambiguationData":[OSD([subQ1])]}),makeQuery(id+"F8.opExtrude","SWEPT_FACE",FACE,{"disambiguationData":[OSD([subQ0]),TDD([makeQuery(id+"F7.imprint","IMPRINT",EDGE,{"disambiguationData":[TD([[makeQuery(id+"F7.imprint","INTERSECT",VERTEX,{"derivedFrom":[sQuery(id+"F7.wireOp",EDGE,"E18.1.0.3"),subQ0]}),-1.0]])],"derivedFrom":subQ0}),makeQuery(id+"F7.imprint","IMPRINT",EDGE,{"disambiguationData":[TD([[makeQuery(id+"F7.imprint","INTERSECT",VERTEX,{"derivedFrom":[subQ0,sQuery(id+"F7.wireOp",EDGE,"E18.1.0.19")]}),1.0]])],"derivedFrom":subQ0})])]})]});}
            var Q4;
            Q4=makeQuery(id+"F8.boolean.opBoolean","COPY",EDGE,{"derivedFrom":makeQuery(id+"F8.opExtrude","SWEPT_EDGE",EDGE,{"disambiguationData":[OSD([sQuery(id+"F7.wireOp",EDGE,"E18.1.0.10"),sQuery(id+"F7.wireOp",EDGE,"E18.1.0.19")])]})});
            var Q5;
            {var subQ0=sQuery(id+"F7.wireOp",EDGE,"E18.1.0.3");var subQ1=sQuery(id+"F0.wireOp",EDGE,"E1");Q5=makeQuery(id+"F8.boolean.opBoolean","INTERSECT",EDGE,{"derivedFrom":[makeQuery(id+"F1.opExtrude","SWEPT_FACE",FACE,{"disambiguationData":[OSD([subQ1])]}),makeQuery(id+"F8.opExtrude","SWEPT_FACE",FACE,{"disambiguationData":[OSD([subQ0]),TDD([makeQuery(id+"F7.imprint","IMPRINT",EDGE,{"disambiguationData":[TD([[makeQuery(id+"F7.imprint","INTERSECT",VERTEX,{"derivedFrom":[subQ0,sQuery(id+"F7.wireOp",EDGE,"E18.1.0.10")]}),-1.0]])],"derivedFrom":subQ0}),makeQuery(id+"F7.imprint","IMPRINT",EDGE,{"disambiguationData":[TD([[makeQuery(id+"F7.imprint","INTERSECT",VERTEX,{"derivedFrom":[subQ0,sQuery(id+"F7.wireOp",EDGE,"E18.1.0.13")]}),1.0]])],"derivedFrom":subQ0})])]})]});}
            var Q6;
            Q6=makeQuery(id+"F8.boolean.opBoolean","COPY",EDGE,{"derivedFrom":makeQuery(id+"F8.opExtrude","SWEPT_EDGE",EDGE,{"disambiguationData":[OSD([sQuery(id+"F7.wireOp",EDGE,"E18.1.0.3"),sQuery(id+"F7.wireOp",EDGE,"E18.1.0.13")])]})});
            var Q7;
            {var subQ0=sQuery(id+"F7.wireOp",EDGE,"E18.1.0.6");var subQ1=sQuery(id+"F0.wireOp",EDGE,"E1");Q7=makeQuery(id+"F8.boolean.opBoolean","INTERSECT",EDGE,{"derivedFrom":[makeQuery(id+"F1.opExtrude","SWEPT_FACE",FACE,{"disambiguationData":[OSD([subQ1])]}),makeQuery(id+"F8.opExtrude","SWEPT_FACE",FACE,{"disambiguationData":[OSD([subQ0]),TDD([makeQuery(id+"F7.imprint","IMPRINT",EDGE,{"disambiguationData":[TD([[makeQuery(id+"F7.imprint","INTERSECT",VERTEX,{"derivedFrom":[sQuery(id+"F7.wireOp",EDGE,"E18.1.0.0"),subQ0]}),-1.0]])],"derivedFrom":subQ0}),makeQuery(id+"F7.imprint","IMPRINT",EDGE,{"disambiguationData":[TD([[makeQuery(id+"F7.imprint","INTERSECT",VERTEX,{"derivedFrom":[subQ0,sQuery(id+"F7.wireOp",EDGE,"E18.1.0.17")]}),1.0]])],"derivedFrom":subQ0})])]})]});}
            var Q8;
            Q8=makeQuery(id+"F8.boolean.opBoolean","COPY",EDGE,{"derivedFrom":makeQuery(id+"F8.opExtrude","SWEPT_EDGE",EDGE,{"disambiguationData":[OSD([sQuery(id+"F7.wireOp",EDGE,"E18.1.0.6"),sQuery(id+"F7.wireOp",EDGE,"E18.1.0.17")])]})});
            var Q9;
            Q9=makeQuery(id+"F8.boolean.opBoolean","COPY",EDGE,{"derivedFrom":makeQuery(id+"F8.opExtrude","SWEPT_EDGE",EDGE,{"disambiguationData":[OSD([sQuery(id+"F7.wireOp",EDGE,"E18.1.0.9"),sQuery(id+"F7.wireOp",EDGE,"E18.1.0.19")])]})});
            var Q10;
            Q10=makeQuery(id+"F8.boolean.opBoolean","COPY",EDGE,{"derivedFrom":makeQuery(id+"F8.opExtrude","SWEPT_EDGE",EDGE,{"disambiguationData":[OSD([sQuery(id+"F7.wireOp",EDGE,"E18.1.0.0"),sQuery(id+"F7.wireOp",EDGE,"E18.1.0.15")])]})});
            var Q11;
            {var subQ0=sQuery(id+"F7.wireOp",EDGE,"E18.1.0.0");var subQ1=sQuery(id+"F0.wireOp",EDGE,"E1");Q11=makeQuery(id+"F8.boolean.opBoolean","INTERSECT",EDGE,{"derivedFrom":[makeQuery(id+"F1.opExtrude","SWEPT_FACE",FACE,{"disambiguationData":[OSD([subQ1])]}),makeQuery(id+"F8.opExtrude","SWEPT_FACE",FACE,{"disambiguationData":[OSD([subQ0]),TDD([makeQuery(id+"F7.imprint","IMPRINT",EDGE,{"disambiguationData":[TD([[makeQuery(id+"F7.imprint","INTERSECT",VERTEX,{"derivedFrom":[subQ0,sQuery(id+"F7.wireOp",EDGE,"E18.1.0.15")]}),-1.0]])],"derivedFrom":subQ0}),makeQuery(id+"F7.imprint","IMPRINT",EDGE,{"disambiguationData":[TD([[makeQuery(id+"F7.imprint","INTERSECT",VERTEX,{"derivedFrom":[subQ0,sQuery(id+"F7.wireOp",EDGE,"E18.1.0.1")]}),1.0]])],"derivedFrom":subQ0})])]})]});}
            var Q12;
            {var subQ0=sQuery(id+"F7.wireOp",EDGE,"E18.1.0.1");var subQ1=sQuery(id+"F0.wireOp",EDGE,"E1");Q12=makeQuery(id+"F8.boolean.opBoolean","INTERSECT",EDGE,{"derivedFrom":[makeQuery(id+"F1.opExtrude","SWEPT_FACE",FACE,{"disambiguationData":[OSD([subQ1])]}),makeQuery(id+"F8.opExtrude","SWEPT_FACE",FACE,{"disambiguationData":[OSD([subQ0]),TDD([makeQuery(id+"F7.imprint","IMPRINT",EDGE,{"disambiguationData":[TD([[makeQuery(id+"F7.imprint","INTERSECT",VERTEX,{"derivedFrom":[sQuery(id+"F7.wireOp",EDGE,"E18.1.0.0"),subQ0]}),-1.0]])],"derivedFrom":subQ0}),makeQuery(id+"F7.imprint","IMPRINT",EDGE,{"disambiguationData":[TD([[makeQuery(id+"F7.imprint","INTERSECT",VERTEX,{"derivedFrom":[subQ0,sQuery(id+"F7.wireOp",EDGE,"E18.1.0.13")]}),1.0]])],"derivedFrom":subQ0})])]})]});}
            var Q13;
            Q13=makeQuery(id+"F8.boolean.opBoolean","COPY",EDGE,{"derivedFrom":makeQuery(id+"F8.opExtrude","SWEPT_EDGE",EDGE,{"disambiguationData":[OSD([sQuery(id+"F7.wireOp",EDGE,"E18.1.0.1"),sQuery(id+"F7.wireOp",EDGE,"E18.1.0.13")])]})});
            var Q14;
            Q14=makeQuery(id+"F8.boolean.opBoolean","COPY",EDGE,{"derivedFrom":makeQuery(id+"F8.opExtrude","SWEPT_EDGE",EDGE,{"disambiguationData":[OSD([sQuery(id+"F7.wireOp",EDGE,"E18.1.0.4"),sQuery(id+"F7.wireOp",EDGE,"E18.1.0.15")])]})});
            var Q15;
            {var subQ0=sQuery(id+"F7.wireOp",EDGE,"E18.1.0.4");var subQ1=sQuery(id+"F0.wireOp",EDGE,"E1");Q15=makeQuery(id+"F8.boolean.opBoolean","INTERSECT",EDGE,{"derivedFrom":[makeQuery(id+"F1.opExtrude","SWEPT_FACE",FACE,{"disambiguationData":[OSD([subQ1])]}),makeQuery(id+"F8.opExtrude","SWEPT_FACE",FACE,{"disambiguationData":[OSD([subQ0]),TDD([makeQuery(id+"F7.imprint","IMPRINT",EDGE,{"disambiguationData":[TD([[makeQuery(id+"F7.imprint","INTERSECT",VERTEX,{"derivedFrom":[subQ0,sQuery(id+"F7.wireOp",EDGE,"E18.1.0.15")]}),-1.0]])],"derivedFrom":subQ0}),makeQuery(id+"F7.imprint","IMPRINT",EDGE,{"disambiguationData":[TD([[makeQuery(id+"F7.imprint","INTERSECT",VERTEX,{"derivedFrom":[subQ0,sQuery(id+"F7.wireOp",EDGE,"E18.1.0.7")]}),1.0]])],"derivedFrom":subQ0})])]})]});}
            var Q16;
            Q16=makeQuery(id+"F8.boolean.opBoolean","COPY",EDGE,{"derivedFrom":makeQuery(id+"F8.opExtrude","SWEPT_EDGE",EDGE,{"disambiguationData":[OSD([sQuery(id+"F7.wireOp",EDGE,"E18.1.0.7"),sQuery(id+"F7.wireOp",EDGE,"E18.1.0.18")])]})});
            var Q17;
            {var subQ0=sQuery(id+"F7.wireOp",EDGE,"E18.1.0.7");var subQ1=sQuery(id+"F0.wireOp",EDGE,"E1");Q17=makeQuery(id+"F8.boolean.opBoolean","INTERSECT",EDGE,{"derivedFrom":[makeQuery(id+"F1.opExtrude","SWEPT_FACE",FACE,{"disambiguationData":[OSD([subQ1])]}),makeQuery(id+"F8.opExtrude","SWEPT_FACE",FACE,{"disambiguationData":[OSD([subQ0]),TDD([makeQuery(id+"F7.imprint","IMPRINT",EDGE,{"disambiguationData":[TD([[makeQuery(id+"F7.imprint","INTERSECT",VERTEX,{"derivedFrom":[subQ0,sQuery(id+"F7.wireOp",EDGE,"E18.1.0.18")]}),-1.0]])],"derivedFrom":subQ0}),makeQuery(id+"F7.imprint","IMPRINT",EDGE,{"disambiguationData":[TD([[makeQuery(id+"F7.imprint","INTERSECT",VERTEX,{"derivedFrom":[sQuery(id+"F7.wireOp",EDGE,"E18.1.0.4"),subQ0]}),1.0]])],"derivedFrom":subQ0})])]})]});}
            var Q18;
            Q18=makeQuery(id+"F8.boolean.opBoolean","COPY",EDGE,{"derivedFrom":makeQuery(id+"F8.opExtrude","SWEPT_EDGE",EDGE,{"disambiguationData":[OSD([sQuery(id+"F7.wireOp",EDGE,"E18.1.0.6"),sQuery(id+"F7.wireOp",EDGE,"E18.1.0.18")])]})});
            var Q19;
            {var subQ0=sQuery(id+"F7.wireOp",EDGE,"E18.1.0.6");var subQ1=sQuery(id+"F0.wireOp",EDGE,"E1");Q19=makeQuery(id+"F8.boolean.opBoolean","INTERSECT",EDGE,{"derivedFrom":[makeQuery(id+"F1.opExtrude","SWEPT_FACE",FACE,{"disambiguationData":[OSD([subQ1])]}),makeQuery(id+"F8.opExtrude","SWEPT_FACE",FACE,{"disambiguationData":[OSD([subQ0]),TDD([makeQuery(id+"F7.imprint","IMPRINT",EDGE,{"disambiguationData":[TD([[makeQuery(id+"F7.imprint","INTERSECT",VERTEX,{"derivedFrom":[subQ0,sQuery(id+"F7.wireOp",EDGE,"E18.1.0.18")]}),-1.0]])],"derivedFrom":subQ0}),makeQuery(id+"F7.imprint","IMPRINT",EDGE,{"disambiguationData":[TD([[makeQuery(id+"F7.imprint","INTERSECT",VERTEX,{"derivedFrom":[subQ0,sQuery(id+"F7.wireOp",EDGE,"E18.1.0.10")]}),1.0]])],"derivedFrom":subQ0})])]})]});}
            var Q20;
            {var subQ0=sQuery(id+"F7.wireOp",EDGE,"E18.1.0.10");var subQ1=sQuery(id+"F0.wireOp",EDGE,"E1");Q20=makeQuery(id+"F8.boolean.opBoolean","INTERSECT",EDGE,{"derivedFrom":[makeQuery(id+"F1.opExtrude","SWEPT_FACE",FACE,{"disambiguationData":[OSD([subQ1])]}),makeQuery(id+"F8.opExtrude","SWEPT_FACE",FACE,{"disambiguationData":[OSD([subQ0]),TDD([makeQuery(id+"F7.imprint","IMPRINT",EDGE,{"disambiguationData":[TD([[makeQuery(id+"F7.imprint","INTERSECT",VERTEX,{"derivedFrom":[subQ0,sQuery(id+"F7.wireOp",EDGE,"E18.1.0.20")]}),-1.0]])],"derivedFrom":subQ0}),makeQuery(id+"F7.imprint","IMPRINT",EDGE,{"disambiguationData":[TD([[makeQuery(id+"F7.imprint","INTERSECT",VERTEX,{"derivedFrom":[sQuery(id+"F7.wireOp",EDGE,"E18.1.0.6"),subQ0]}),1.0]])],"derivedFrom":subQ0})])]})]});}
            var Q21;
            Q21=makeQuery(id+"F8.boolean.opBoolean","COPY",EDGE,{"derivedFrom":makeQuery(id+"F8.opExtrude","SWEPT_EDGE",EDGE,{"disambiguationData":[OSD([sQuery(id+"F7.wireOp",EDGE,"E18.1.0.10"),sQuery(id+"F7.wireOp",EDGE,"E18.1.0.20")])]})});
            var Q22;
            Q22=makeQuery(id+"F8.boolean.opBoolean","COPY",EDGE,{"derivedFrom":makeQuery(id+"F8.opExtrude","SWEPT_EDGE",EDGE,{"disambiguationData":[OSD([sQuery(id+"F7.wireOp",EDGE,"E18.1.0.9"),sQuery(id+"F7.wireOp",EDGE,"E18.1.0.20")])]})});
            var Q23;
            {var subQ0=sQuery(id+"F7.wireOp",EDGE,"E18.1.0.9");var subQ1=sQuery(id+"F0.wireOp",EDGE,"E1");Q23=makeQuery(id+"F8.boolean.opBoolean","INTERSECT",EDGE,{"derivedFrom":[makeQuery(id+"F1.opExtrude","SWEPT_FACE",FACE,{"disambiguationData":[OSD([subQ1])]}),makeQuery(id+"F8.opExtrude","SWEPT_FACE",FACE,{"disambiguationData":[OSD([subQ0]),TDD([makeQuery(id+"F7.imprint","IMPRINT",EDGE,{"disambiguationData":[TD([[makeQuery(id+"F7.imprint","INTERSECT",VERTEX,{"derivedFrom":[subQ0,sQuery(id+"F7.wireOp",EDGE,"E18.1.0.20")]}),-1.0]])],"derivedFrom":subQ0}),makeQuery(id+"F7.imprint","IMPRINT",EDGE,{"disambiguationData":[TD([[makeQuery(id+"F7.imprint","INTERSECT",VERTEX,{"derivedFrom":[sQuery(id+"F7.wireOp",EDGE,"E18.1.0.1"),subQ0]}),1.0]])],"derivedFrom":subQ0})])]})]});}
            var Q24;
            Q24=makeQuery(id+"F8.boolean.opBoolean","COPY",EDGE,{"derivedFrom":makeQuery(id+"F8.opExtrude","SWEPT_EDGE",EDGE,{"disambiguationData":[OSD([sQuery(id+"F7.wireOp",EDGE,"E18.1.0.1"),sQuery(id+"F7.wireOp",EDGE,"E18.1.0.14")])]})});
            var Q25;
            {var subQ0=sQuery(id+"F7.wireOp",EDGE,"E18.1.0.1");var subQ1=sQuery(id+"F0.wireOp",EDGE,"E1");Q25=makeQuery(id+"F8.boolean.opBoolean","INTERSECT",EDGE,{"derivedFrom":[makeQuery(id+"F1.opExtrude","SWEPT_FACE",FACE,{"disambiguationData":[OSD([subQ1])]}),makeQuery(id+"F8.opExtrude","SWEPT_FACE",FACE,{"disambiguationData":[OSD([subQ0]),TDD([makeQuery(id+"F7.imprint","IMPRINT",EDGE,{"disambiguationData":[TD([[makeQuery(id+"F7.imprint","INTERSECT",VERTEX,{"derivedFrom":[subQ0,sQuery(id+"F7.wireOp",EDGE,"E18.1.0.14")]}),-1.0]])],"derivedFrom":subQ0}),makeQuery(id+"F7.imprint","IMPRINT",EDGE,{"disambiguationData":[TD([[makeQuery(id+"F7.imprint","INTERSECT",VERTEX,{"derivedFrom":[subQ0,sQuery(id+"F7.wireOp",EDGE,"E18.1.0.9")]}),1.0]])],"derivedFrom":subQ0})])]})]});}
            var Q26;
            {var subQ0=sQuery(id+"F7.wireOp",EDGE,"E18.1.0.3");var subQ1=sQuery(id+"F0.wireOp",EDGE,"E1");Q26=makeQuery(id+"F8.boolean.opBoolean","INTERSECT",EDGE,{"derivedFrom":[makeQuery(id+"F1.opExtrude","SWEPT_FACE",FACE,{"disambiguationData":[OSD([subQ1])]}),makeQuery(id+"F8.opExtrude","SWEPT_FACE",FACE,{"disambiguationData":[OSD([subQ0]),TDD([makeQuery(id+"F7.imprint","IMPRINT",EDGE,{"disambiguationData":[TD([[makeQuery(id+"F7.imprint","INTERSECT",VERTEX,{"derivedFrom":[subQ0,sQuery(id+"F7.wireOp",EDGE,"E18.1.0.14")]}),-1.0]])],"derivedFrom":subQ0}),makeQuery(id+"F7.imprint","IMPRINT",EDGE,{"disambiguationData":[TD([[makeQuery(id+"F7.imprint","INTERSECT",VERTEX,{"derivedFrom":[subQ0,sQuery(id+"F7.wireOp",EDGE,"E18.1.0.4")]}),1.0]])],"derivedFrom":subQ0})])]})]});}
            var Q27;
            Q27=makeQuery(id+"F8.boolean.opBoolean","COPY",EDGE,{"derivedFrom":makeQuery(id+"F8.opExtrude","SWEPT_EDGE",EDGE,{"disambiguationData":[OSD([sQuery(id+"F7.wireOp",EDGE,"E18.1.0.3"),sQuery(id+"F7.wireOp",EDGE,"E18.1.0.14")])]})});
            var Q28;
            Q28=makeQuery(id+"F8.boolean.opBoolean","COPY",EDGE,{"derivedFrom":makeQuery(id+"F8.opExtrude","SWEPT_EDGE",EDGE,{"disambiguationData":[OSD([sQuery(id+"F7.wireOp",EDGE,"E18.1.0.4"),sQuery(id+"F7.wireOp",EDGE,"E18.1.0.16")])]})});
            var Q29;
            {var subQ0=sQuery(id+"F7.wireOp",EDGE,"E18.1.0.4");var subQ1=sQuery(id+"F0.wireOp",EDGE,"E1");Q29=makeQuery(id+"F8.boolean.opBoolean","INTERSECT",EDGE,{"derivedFrom":[makeQuery(id+"F1.opExtrude","SWEPT_FACE",FACE,{"disambiguationData":[OSD([subQ1])]}),makeQuery(id+"F8.opExtrude","SWEPT_FACE",FACE,{"disambiguationData":[OSD([subQ0]),TDD([makeQuery(id+"F7.imprint","IMPRINT",EDGE,{"disambiguationData":[TD([[makeQuery(id+"F7.imprint","INTERSECT",VERTEX,{"derivedFrom":[sQuery(id+"F7.wireOp",EDGE,"E18.1.0.3"),subQ0]}),-1.0]])],"derivedFrom":subQ0}),makeQuery(id+"F7.imprint","IMPRINT",EDGE,{"disambiguationData":[TD([[makeQuery(id+"F7.imprint","INTERSECT",VERTEX,{"derivedFrom":[subQ0,sQuery(id+"F7.wireOp",EDGE,"E18.1.0.16")]}),1.0]])],"derivedFrom":subQ0})])]})]});}
            var Q30;
            Q30=makeQuery(id+"F8.boolean.opBoolean","COPY",EDGE,{"derivedFrom":makeQuery(id+"F8.opExtrude","SWEPT_EDGE",EDGE,{"disambiguationData":[OSD([sQuery(id+"F7.wireOp",EDGE,"E18.1.0.0"),sQuery(id+"F7.wireOp",EDGE,"E18.1.0.16")])]})});
            var Q31;
            {var subQ0=sQuery(id+"F7.wireOp",EDGE,"E18.1.0.0");var subQ1=sQuery(id+"F0.wireOp",EDGE,"E1");Q31=makeQuery(id+"F8.boolean.opBoolean","INTERSECT",EDGE,{"derivedFrom":[makeQuery(id+"F1.opExtrude","SWEPT_FACE",FACE,{"disambiguationData":[OSD([subQ1])]}),makeQuery(id+"F8.opExtrude","SWEPT_FACE",FACE,{"disambiguationData":[OSD([subQ0]),TDD([makeQuery(id+"F7.imprint","IMPRINT",EDGE,{"disambiguationData":[TD([[makeQuery(id+"F7.imprint","INTERSECT",VERTEX,{"derivedFrom":[subQ0,sQuery(id+"F7.wireOp",EDGE,"E18.1.0.6")]}),-1.0]])],"derivedFrom":subQ0}),makeQuery(id+"F7.imprint","IMPRINT",EDGE,{"disambiguationData":[TD([[makeQuery(id+"F7.imprint","INTERSECT",VERTEX,{"derivedFrom":[subQ0,sQuery(id+"F7.wireOp",EDGE,"E18.1.0.16")]}),1.0]])],"derivedFrom":subQ0})])]})]});}
            fillet(context, id + "F10", {"entities" : qUnion([Q0, Q1, Q2, Q3, Q4, Q5, Q6, Q7, Q8, Q9, Q10, Q11, Q12, Q13, Q14, Q15, Q16, Q17, Q18, Q19, Q20, Q21, Q22, Q23, Q24, Q25, Q26, Q27, Q28, Q29, Q30, Q31]), "radius" : 0.5 * mm, "tangentPropagation" : true, "allowEdgeOverflow" : false});
        }
        {
            var Q0;
            Q0=makeQuery(id+"F1.opExtrude","SWEPT_EDGE",EDGE,{"disambiguationData":[OSD([sQuery(id+"F0.wireOp",EDGE,"E5.bottom"),sQuery(id+"F0.wireOp",EDGE,"E5.left")])]});
            var Q1;
            Q1=makeQuery(id+"F1.opExtrude","SWEPT_EDGE",EDGE,{"disambiguationData":[OSD([sQuery(id+"F0.wireOp",EDGE,"E5.bottom"),sQuery(id+"F0.wireOp",EDGE,"E5.right")])]});
            fillet(context, id + "F11", {"entities" : qUnion([Q0, Q1]), "radius" : 0.5 * mm, "tangentPropagation" : true, "allowEdgeOverflow" : false});
        }
        {
            var Q0;
            Q0=makeQuery(id+"F1.opExtrude","CAP_FACE",FACE,{"disambiguationData":[OSD([sQuery(id+"F0.wireOp",EDGE,"E0"),sQuery(id+"F0.wireOp",EDGE,"E1"),sQuery(id+"F0.wireOp",EDGE,"E2"),sQuery(id+"F0.wireOp",EDGE,"E5.bottom"),sQuery(id+"F0.wireOp",EDGE,"E5.top"),sQuery(id+"F0.wireOp",EDGE,"E5.left"),sQuery(id+"F0.wireOp",EDGE,"E5.right")])],"isStart":false});
            var sketch = newSketch(context, id + "F12", { "sketchPlane" : qUnion([Q0])});
            skCircle(sketch, "E19", {"center": v(0, 0) * mm, "radius": 11.18 * mm});
            skSolve(sketch);
        }
        {
            var Q0;
            Q0 = qSketchRegion(id + "F12", true);
            extrude(context, id + "F13", {"entities" : qUnion([Q0]), "operationType" : NewBodyOperationType.REMOVE, "oppositeDirection" : true, "depth" : 3.56 * mm, "offsetDistance" : 25.4 * mm});
        }
        {
            var Q0;
            Q0=makeQuery(id+"F13.boolean.opBoolean","INTERSECT",EDGE,{"disambiguationData":[OD(0.0)],"derivedFrom":[makeQuery(id+"F1.opExtrude","SWEPT_FACE",FACE,{"disambiguationData":[OSD([sQuery(id+"F0.wireOp",EDGE,"E5.bottom")])]}),makeQuery(id+"F13.opExtrude","SWEPT_FACE",FACE,{"disambiguationData":[OSD([sQuery(id+"F12.wireOp",EDGE,"E19")])]})]});
            var Q1;
            Q1=makeQuery(id+"F13.boolean.opBoolean","INTERSECT",EDGE,{"disambiguationData":[OD(1.0)],"derivedFrom":[makeQuery(id+"F1.opExtrude","SWEPT_FACE",FACE,{"disambiguationData":[OSD([sQuery(id+"F0.wireOp",EDGE,"E5.bottom")])]}),makeQuery(id+"F13.opExtrude","SWEPT_FACE",FACE,{"disambiguationData":[OSD([sQuery(id+"F12.wireOp",EDGE,"E19")])]})]});
            var Q2;
            Q2=makeQuery(id+"F13.boolean.opBoolean","INTERSECT",EDGE,{"disambiguationData":[OD(1.0)],"derivedFrom":[makeQuery(id+"F1.opExtrude","SWEPT_FACE",FACE,{"disambiguationData":[OSD([sQuery(id+"F0.wireOp",EDGE,"E5.top")])]}),makeQuery(id+"F13.opExtrude","SWEPT_FACE",FACE,{"disambiguationData":[OSD([sQuery(id+"F12.wireOp",EDGE,"E19")])]})]});
            var Q3;
            Q3=makeQuery(id+"F13.boolean.opBoolean","INTERSECT",EDGE,{"disambiguationData":[OD(0.0)],"derivedFrom":[makeQuery(id+"F1.opExtrude","SWEPT_FACE",FACE,{"disambiguationData":[OSD([sQuery(id+"F0.wireOp",EDGE,"E5.top")])]}),makeQuery(id+"F13.opExtrude","SWEPT_FACE",FACE,{"disambiguationData":[OSD([sQuery(id+"F12.wireOp",EDGE,"E19")])]})]});
            fillet(context, id + "F14", {"entities" : qUnion([Q0, Q1, Q2, Q3]), "radius" : 0.76 * mm, "tangentPropagation" : true, "allowEdgeOverflow" : false});
        }
    });
